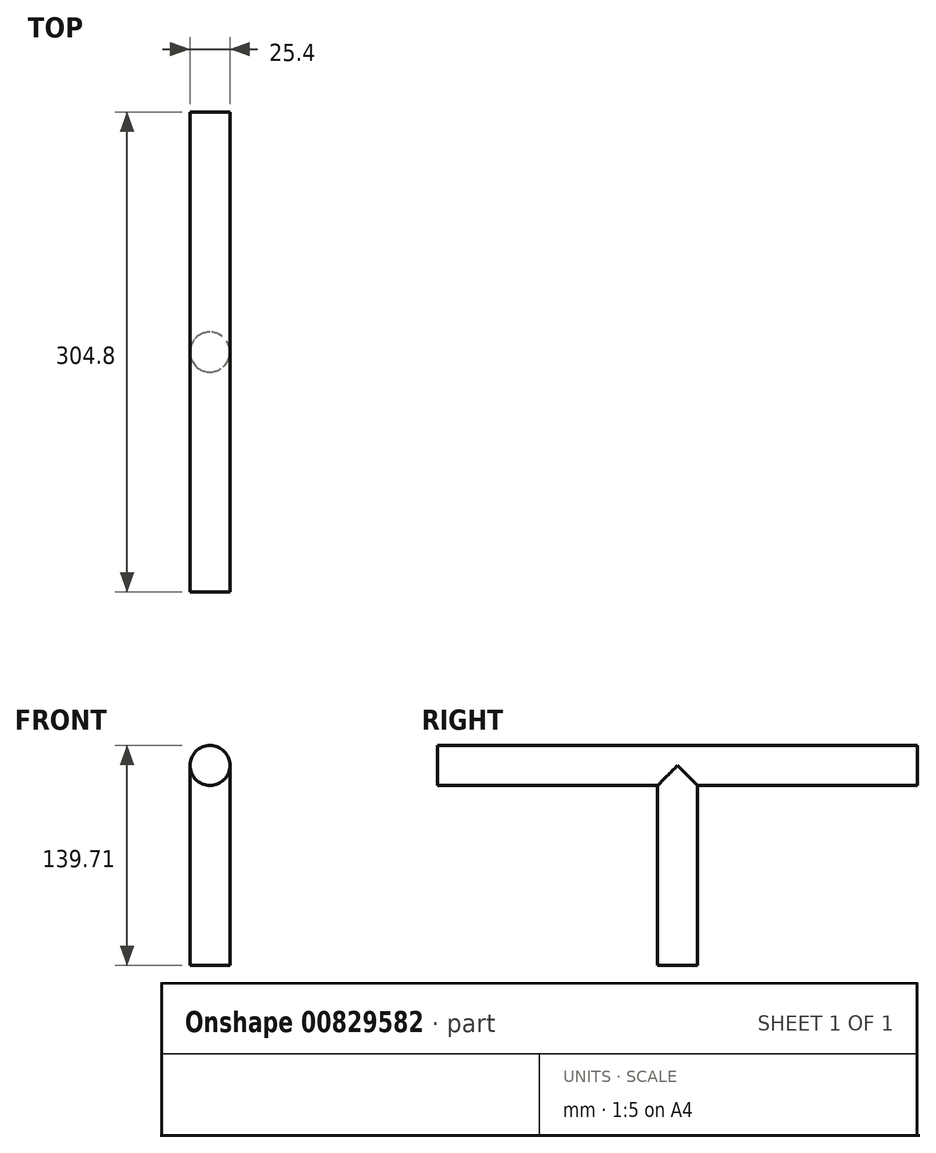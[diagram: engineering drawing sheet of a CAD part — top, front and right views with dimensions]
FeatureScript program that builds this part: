
annotation { "Feature Type Name" : "Feature", "Feature Type Description" : "" }
export const myFeature = defineFeature(function(context is Context, id is Id, definition is map)
    precondition{}
    {
        {
            var Q0;
            Q0=qCreatedBy(makeId("Top.planeOp"),FACE);
            var sketch = newSketch(context, id + "F0", { "sketchPlane" : qUnion([Q0])});
            skCircle(sketch, "E0", {"center": v(0, 0) * mm, "radius": 12.7 * mm});
            skSolve(sketch);
        }
        {
            var Q0;
            Q0=qCreatedBy(makeId("Right.planeOp"),FACE);
            var sketch = newSketch(context, id + "F1", { "sketchPlane" : qUnion([Q0])});
            skLineSegment(sketch, "E1", {"start": v(0, 0) * mm, "end": v(0, 127) * mm});
            skSolve(sketch);
        }
        {
            var Q0;
            Q0=sQuery(id+"F1.wireOp",EDGE,"E1");
            var Q1;
            Q1=sQuery(id+"F1.wireOp",VERTEX,"E1.end");
            cPlane(context, id + "F2", {"entities" : qUnion([Q0, Q1]), "cplaneType" : CPlaneType.LINE_POINT, "offset" : 25.4 * mm, "width" : 152.4 * mm, "height" : 152.4 * mm});
        }
        {
            var Q0;
            Q0=qCreatedBy(id+"F2.planeOp",FACE);
            var sketch = newSketch(context, id + "F3", { "sketchPlane" : qUnion([Q0])});
            skLineSegment(sketch, "E2", {"start": v(0, 0) * mm, "end": v(0, 152.4) * mm});
            skLineSegment(sketch, "E3", {"start": v(0, 0) * mm, "end": v(0, -152.4) * mm});
            skSolve(sketch);
        }
        {
            var Q0;
            Q0=makeQuery(id+"F0.imprint","IMPRINT",FACE,{"disambiguationData":[TD([[makeQuery(id+"F0.imprint","IMPRINT",EDGE,{"derivedFrom":sQuery(id+"F0.wireOp",EDGE,"E0")}),1.0]])]});
            var Q1;
            Q1=sQuery(id+"F1.wireOp",EDGE,"E1");
            sweep(context, id + "F4", {"profiles" : qUnion([Q0]), "path" : qUnion([Q1])});
        }
        {
            var Q0;
            Q0=sQuery(id+"F3.wireOp",VERTEX,"E3.end");
            var Q1;
            Q1=sQuery(id+"F3.wireOp",EDGE,"E3");
            cPlane(context, id + "F5", {"entities" : qUnion([Q0, Q1]), "cplaneType" : CPlaneType.LINE_POINT, "offset" : 25.4 * mm, "width" : 152.4 * mm, "height" : 152.4 * mm});
        }
        {
            var Q0;
            Q0=qCreatedBy(id+"F5.planeOp",FACE);
            var sketch = newSketch(context, id + "F6", { "sketchPlane" : qUnion([Q0])});
            skCircle(sketch, "E4", {"center": v(0, 127.01) * mm, "radius": 12.7 * mm});
            skSolve(sketch);
        }
        {
            var Q0;
            Q0=makeQuery(id+"F6.imprint","IMPRINT",FACE,{"disambiguationData":[TD([[makeQuery(id+"F6.imprint","IMPRINT",EDGE,{"derivedFrom":sQuery(id+"F6.wireOp",EDGE,"E4")}),1.0]])]});
            var Q1;
            Q1=sQuery(id+"F3.wireOp",EDGE,"E3");
            var Q2;
            Q2=sQuery(id+"F3.wireOp",EDGE,"E2");
            sweep(context, id + "F7", {"operationType" : NewBodyOperationType.ADD, "profiles" : qUnion([Q0]), "path" : qUnion([Q1, Q2])});
        }
    });
